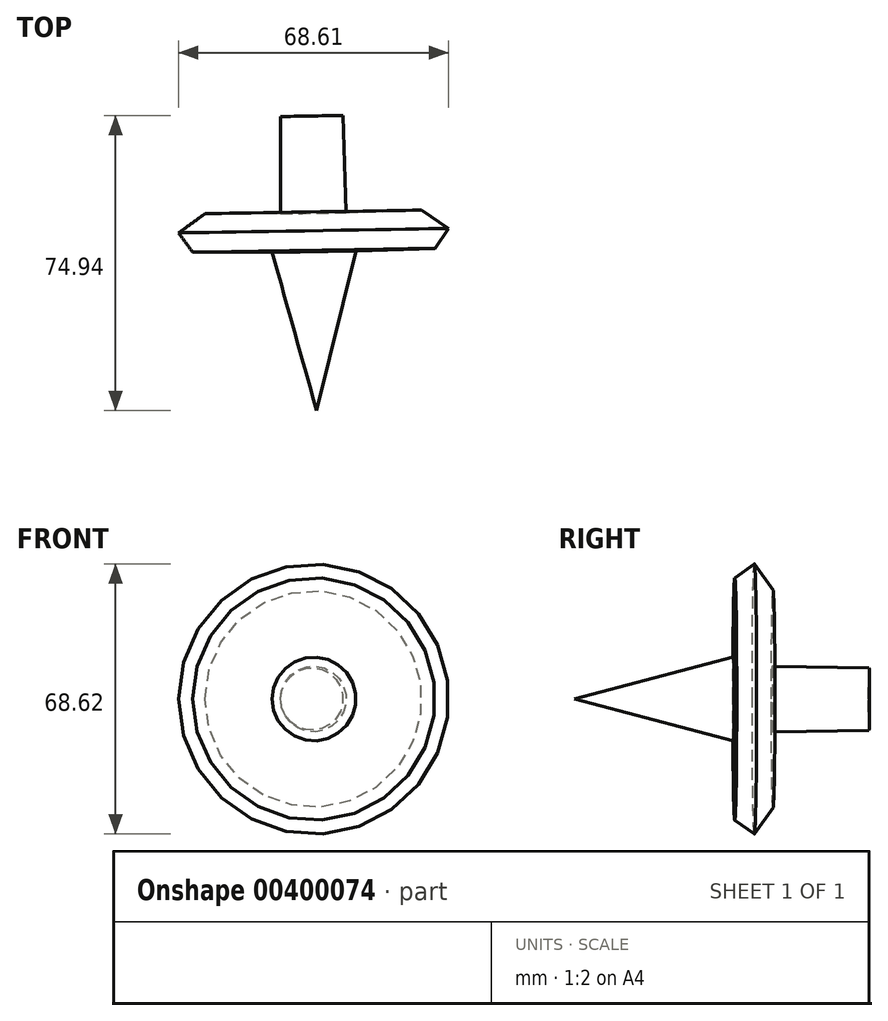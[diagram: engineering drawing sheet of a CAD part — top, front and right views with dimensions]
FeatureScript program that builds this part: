
annotation { "Feature Type Name" : "Feature", "Feature Type Description" : "" }
export const myFeature = defineFeature(function(context is Context, id is Id, definition is map)
    precondition{}
    {
        {
            var Q0;
            Q0=qCreatedBy(makeId("Top.planeOp"),FACE);
            var sketch = newSketch(context, id + "F0", { "sketchPlane" : qUnion([Q0])});
            skLineSegment(sketch, "E0", {"start": v(-37.8, 57.15) * mm, "end": v(-29.87, 57.15) * mm});
            skLineSegment(sketch, "E1", {"start": v(-37.8, 57.15) * mm, "end": v(-37.8, 32.46) * mm});
            skLineSegment(sketch, "E2", {"start": v(-37.8, 32.46) * mm, "end": v(-28.65, 32.46) * mm});
            skLineSegment(sketch, "E3", {"start": v(-37.8, 32.46) * mm, "end": v(-57, 32.46) * mm});
            skLineSegment(sketch, "E4", {"start": v(-57, 32.46) * mm, "end": v(-63.7, 27.58) * mm});
            skLineSegment(sketch, "E5", {"start": v(-63.7, 27.58) * mm, "end": v(-60.12, 22.65) * mm});
            skLineSegment(sketch, "E6", {"start": v(-60.12, 22.65) * mm, "end": v(-28.35, 22.65) * mm});
            skLineSegment(sketch, "E7", {"start": v(-39.93, 22.65) * mm, "end": v(-28.65, -17.53) * mm});
            skLineSegment(sketch, "E8", {"start": v(-29.87, 57.15) * mm, "end": v(-28.65, -17.53) * mm});
            skSolve(sketch);
        }
        {
            var Q0;
            {var subQ0=sQuery(id+"F0.wireOp",EDGE,"E0");Q0=makeQuery(id+"F0.imprint","IMPRINT",FACE,{"disambiguationData":[TD([[makeQuery(id+"F0.imprint","IMPRINT",EDGE,{"derivedFrom":subQ0}),-1.0]])]});}
            var Q1;
            {var subQ1=sQuery(id+"F0.wireOp",EDGE,"E3");Q1=makeQuery(id+"F0.imprint","IMPRINT",FACE,{"disambiguationData":[TD([[makeQuery(id+"F0.imprint","IMPRINT",EDGE,{"derivedFrom":subQ1}),1.0]])]});}
            var Q2;
            {var subQ0=sQuery(id+"F0.wireOp",EDGE,"E7");Q2=makeQuery(id+"F0.imprint","IMPRINT",FACE,{"disambiguationData":[TD([[makeQuery(id+"F0.imprint","IMPRINT",EDGE,{"derivedFrom":subQ0}),1.0]])]});}
            var Q3;
            Q3=sQuery(id+"F0.wireOp",EDGE,"E8");
            revolve(context, id + "F1", {"entities" : qUnion([Q0, Q1, Q2]), "axis" : qUnion([Q3]), "revolveType" : RevolveType.FULL});
        }
    });
